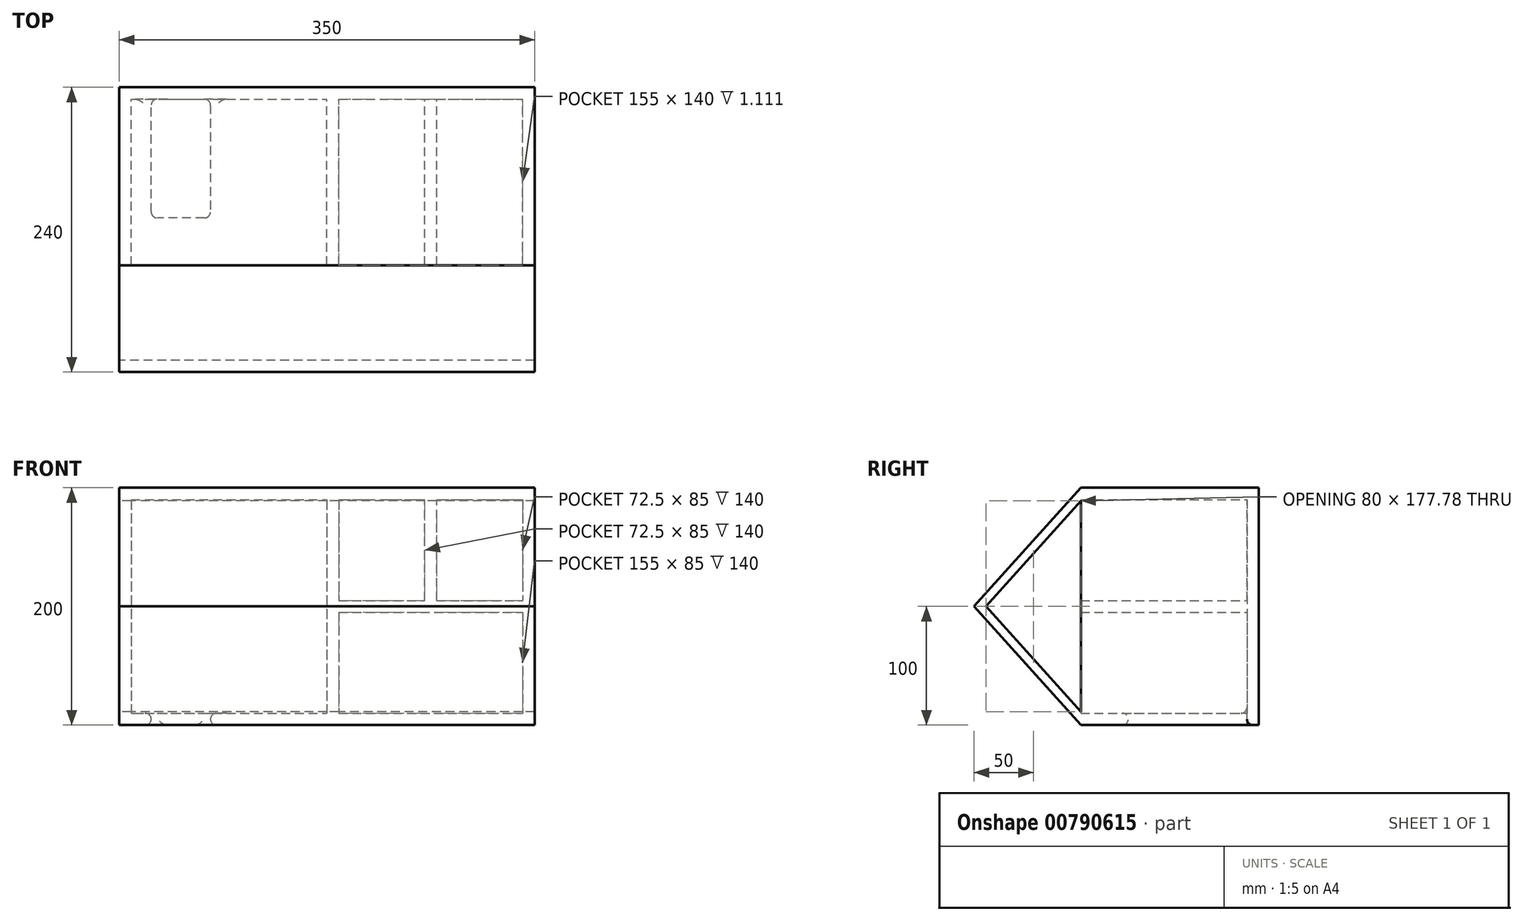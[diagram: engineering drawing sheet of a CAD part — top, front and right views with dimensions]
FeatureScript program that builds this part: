
annotation { "Feature Type Name" : "Feature", "Feature Type Description" : "" }
export const myFeature = defineFeature(function(context is Context, id is Id, definition is map)
    precondition{}
    {
        {
            var Q0;
            Q0=qCreatedBy(makeId("Front.planeOp"),FACE);
            var sketch = newSketch(context, id + "F0", { "sketchPlane" : qUnion([Q0])});
            skLineSegment(sketch, "E0.bottom", {"start": v(0, 0) * mm, "end": v(350, 0) * mm});
            skLineSegment(sketch, "E0.top", {"start": v(0, -200) * mm, "end": v(350, -200) * mm});
            skLineSegment(sketch, "E0.left", {"start": v(0, 0) * mm, "end": v(0, -200) * mm});
            skLineSegment(sketch, "E0.right", {"start": v(350, 0) * mm, "end": v(350, -200) * mm});
            skLineSegment(sketch, "E1.0", {"start": v(10, -10) * mm, "end": v(175, -10) * mm});
            skLineSegment(sketch, "E2.0", {"start": v(10, -10) * mm, "end": v(10, -190) * mm});
            skLineSegment(sketch, "E3", {"start": v(350, -100) * mm, "end": v(483.58, -100) * mm});
            skLineSegment(sketch, "E4.MirrorCS", {"start": v(10, -190) * mm, "end": v(175, -190) * mm});
            skLineSegment(sketch, "E5", {"start": v(175, 0) * mm, "end": v(175, 74.87) * mm});
            skLineSegment(sketch, "E6.MirrorCS", {"start": v(340, -10) * mm, "end": v(340, -95) * mm});
            skPoint(sketch, "E7.orphan", {"position": v(10, 0) * mm});
            skPoint(sketch, "E8.orphan", {"position": v(0, -10) * mm});
            skPoint(sketch, "E9.orphan", {"position": v(340, 0) * mm});
            skPoint(sketch, "E10.orphan", {"position": v(350, -10) * mm});
            skPoint(sketch, "E11.orphan", {"position": v(350, -190) * mm});
            skPoint(sketch, "E12.orphan", {"position": v(340, -200) * mm});
            skPoint(sketch, "E13.orphan", {"position": v(0, -190) * mm});
            skPoint(sketch, "E14.orphan", {"position": v(10, -200) * mm});
            skLineSegment(sketch, "E15", {"start": v(175, -10) * mm, "end": v(175, -190) * mm});
            skLineSegment(sketch, "E16.0", {"start": v(185, -10) * mm, "end": v(185, -95) * mm});
            skLineSegment(sketch, "E17.0", {"start": v(185, -95) * mm, "end": v(257.5, -95) * mm});
            skLineSegment(sketch, "E18.trimOffspring", {"start": v(340, -105) * mm, "end": v(340, -190) * mm});
            skLineSegment(sketch, "E19.trimOffspring", {"start": v(185, -105) * mm, "end": v(185, -190) * mm});
            skLineSegment(sketch, "E20.trimOffspring", {"start": v(185, -190) * mm, "end": v(340, -190) * mm});
            skLineSegment(sketch, "E21.trimOffspring", {"start": v(185, -10) * mm, "end": v(257.5, -10) * mm});
            skLineSegment(sketch, "E22.0", {"start": v(257.5, -95) * mm, "end": v(257.5, -10) * mm});
            skLineSegment(sketch, "E23.MirrorCS", {"start": v(267.5, -95) * mm, "end": v(267.5, -10) * mm});
            skLineSegment(sketch, "E24.trimOffspring", {"start": v(267.5, -10) * mm, "end": v(340, -10) * mm});
            skPoint(sketch, "E25.end.orphan", {"position": v(262.5, -10) * mm});
            skPoint(sketch, "E25.start.orphan", {"position": v(262.5, -95) * mm});
            skLineSegment(sketch, "E26.MirrorCS", {"start": v(185, -105) * mm, "end": v(340, -105) * mm});
            skPoint(sketch, "E27.start.orphan", {"position": v(185, -100) * mm});
            skLineSegment(sketch, "E28.trimOffspring", {"start": v(267.5, -95) * mm, "end": v(340, -95) * mm});
            skPoint(sketch, "E29.orphan", {"position": v(340, -100) * mm});
            skSolve(sketch);
        }
        {
            var Q0;
            {var subQ1=sQuery(id+"F0.wireOp",EDGE,"E0.top");Q0=makeQuery(id+"F0.imprint","IMPRINT",FACE,{"disambiguationData":[TD([[makeQuery(id+"F0.imprint","IMPRINT",EDGE,{"derivedFrom":subQ1}),1.0]])]});}
            extrude(context, id + "F1", {"entities" : qUnion([Q0]), "depth" : 150 * mm, "offsetDistance" : 25 * mm});
        }
        {
            var Q0;
            Q0=makeQuery(id+"F0.imprint","IMPRINT",FACE,{"disambiguationData":[TD([[makeQuery(id+"F0.imprint","IMPRINT",EDGE,{"derivedFrom":sQuery(id+"F0.wireOp",EDGE,"E1.0")}),-1.0]])]});
            var Q1;
            Q1=makeQuery(id+"F0.imprint","IMPRINT",FACE,{"disambiguationData":[TD([[makeQuery(id+"F0.imprint","IMPRINT",EDGE,{"derivedFrom":sQuery(id+"F0.wireOp",EDGE,"E16.0")}),1.0]])]});
            var Q2;
            Q2=makeQuery(id+"F0.imprint","IMPRINT",FACE,{"disambiguationData":[TD([[makeQuery(id+"F0.imprint","IMPRINT",EDGE,{"derivedFrom":sQuery(id+"F0.wireOp",EDGE,"E6.MirrorCS")}),-1.0]])]});
            var Q3;
            Q3=makeQuery(id+"F0.imprint","IMPRINT",FACE,{"disambiguationData":[TD([[makeQuery(id+"F0.imprint","IMPRINT",EDGE,{"derivedFrom":sQuery(id+"F0.wireOp",EDGE,"E18.trimOffspring")}),-1.0]])]});
            extrude(context, id + "F2", {"entities" : qUnion([Q0, Q1, Q2, Q3]), "operationType" : NewBodyOperationType.ADD, "depth" : 10 * mm, "offsetDistance" : 25 * mm});
        }
        {
            var Q0;
            Q0=makeQuery(id+"F1.opExtrude","SWEPT_FACE",FACE,{"disambiguationData":[OSD([sQuery(id+"F0.wireOp",EDGE,"E0.left")])]});
            var sketch = newSketch(context, id + "F3", { "sketchPlane" : qUnion([Q0])});
            skLineSegment(sketch, "E30", {"start": v(240, -100) * mm, "end": v(150, 0) * mm});
            skLineSegment(sketch, "E31", {"start": v(240, -100) * mm, "end": v(150, -200) * mm});
            skPoint(sketch, "E32.start.orphan", {"position": v(150, -100) * mm});
            skLineSegment(sketch, "E33", {"start": v(230, -100) * mm, "end": v(150, -11.11) * mm});
            skLineSegment(sketch, "E34.MirrorCS", {"start": v(230, -100) * mm, "end": v(150, -188.89) * mm});
            skPoint(sketch, "E35.orphan", {"position": v(160, 0) * mm});
            skLineSegment(sketch, "E36", {"start": v(150, 0) * mm, "end": v(150, -11.11) * mm});
            skLineSegment(sketch, "E37", {"start": v(150, -188.89) * mm, "end": v(150, -200) * mm});
            skSolve(sketch);
        }
        {
            var Q0;
            Q0=makeQuery(id+"F3.imprint","IMPRINT",FACE,{"disambiguationData":[TD([[makeQuery(id+"F3.imprint","IMPRINT",EDGE,{"derivedFrom":sQuery(id+"F3.wireOp",EDGE,"E30")}),1.0]])]});
            extrude(context, id + "F4", {"entities" : qUnion([Q0]), "operationType" : NewBodyOperationType.ADD, "oppositeDirection" : true, "depth" : 350 * mm, "offsetDistance" : 25 * mm});
        }
        {
            var Q0;
            Q0=makeQuery(id+"F1.opExtrude","SWEPT_FACE",FACE,{"disambiguationData":[OSD([sQuery(id+"F0.wireOp",EDGE,"E0.top")])]});
            var sketch = newSketch(context, id + "F5", { "sketchPlane" : qUnion([Q0])});
            skLineSegment(sketch, "E38", {"start": v(26.87, 10) * mm, "end": v(26.87, 110) * mm});
            skLineSegment(sketch, "E39", {"start": v(26.87, 110) * mm, "end": v(76.87, 110) * mm});
            skLineSegment(sketch, "E40", {"start": v(76.87, 110) * mm, "end": v(76.87, 10) * mm});
            skLineSegment(sketch, "E41", {"start": v(26.87, 10) * mm, "end": v(76.87, 10) * mm});
            skSolve(sketch);
        }
        {
            var Q0;
            Q0=makeQuery(id+"F5.imprint","IMPRINT",FACE,{"disambiguationData":[TD([[makeQuery(id+"F5.imprint","IMPRINT",EDGE,{"derivedFrom":sQuery(id+"F5.wireOp",EDGE,"E38")}),-1.0]])]});
            extrude(context, id + "F6", {"entities" : qUnion([Q0]), "operationType" : NewBodyOperationType.REMOVE, "oppositeDirection" : true, "depth" : 10 * mm, "offsetDistance" : 25 * mm});
        }
        {
            var Q0;
            Q0=makeQuery(id+"F6.boolean.opBoolean","COPY",FACE,{"derivedFrom":makeQuery(id+"F6.opExtrude","SWEPT_FACE",FACE,{"disambiguationData":[OSD([sQuery(id+"F5.wireOp",EDGE,"E38")])]})});
            var Q1;
            Q1=makeQuery(id+"F6.boolean.opBoolean","COPY",FACE,{"derivedFrom":makeQuery(id+"F6.opExtrude","SWEPT_FACE",FACE,{"disambiguationData":[OSD([sQuery(id+"F5.wireOp",EDGE,"E40")])]})});
            var Q2;
            Q2=makeQuery(id+"F6.boolean.opBoolean","COPY",FACE,{"derivedFrom":makeQuery(id+"F6.opExtrude","SWEPT_FACE",FACE,{"disambiguationData":[OSD([sQuery(id+"F5.wireOp",EDGE,"E39")])]})});
            fillet(context, id + "F7", {"entities" : qUnion([Q0, Q1, Q2]), "radius" : 5 * mm, "tangentPropagation" : true, "allowEdgeOverflow" : false});
        }
    });
